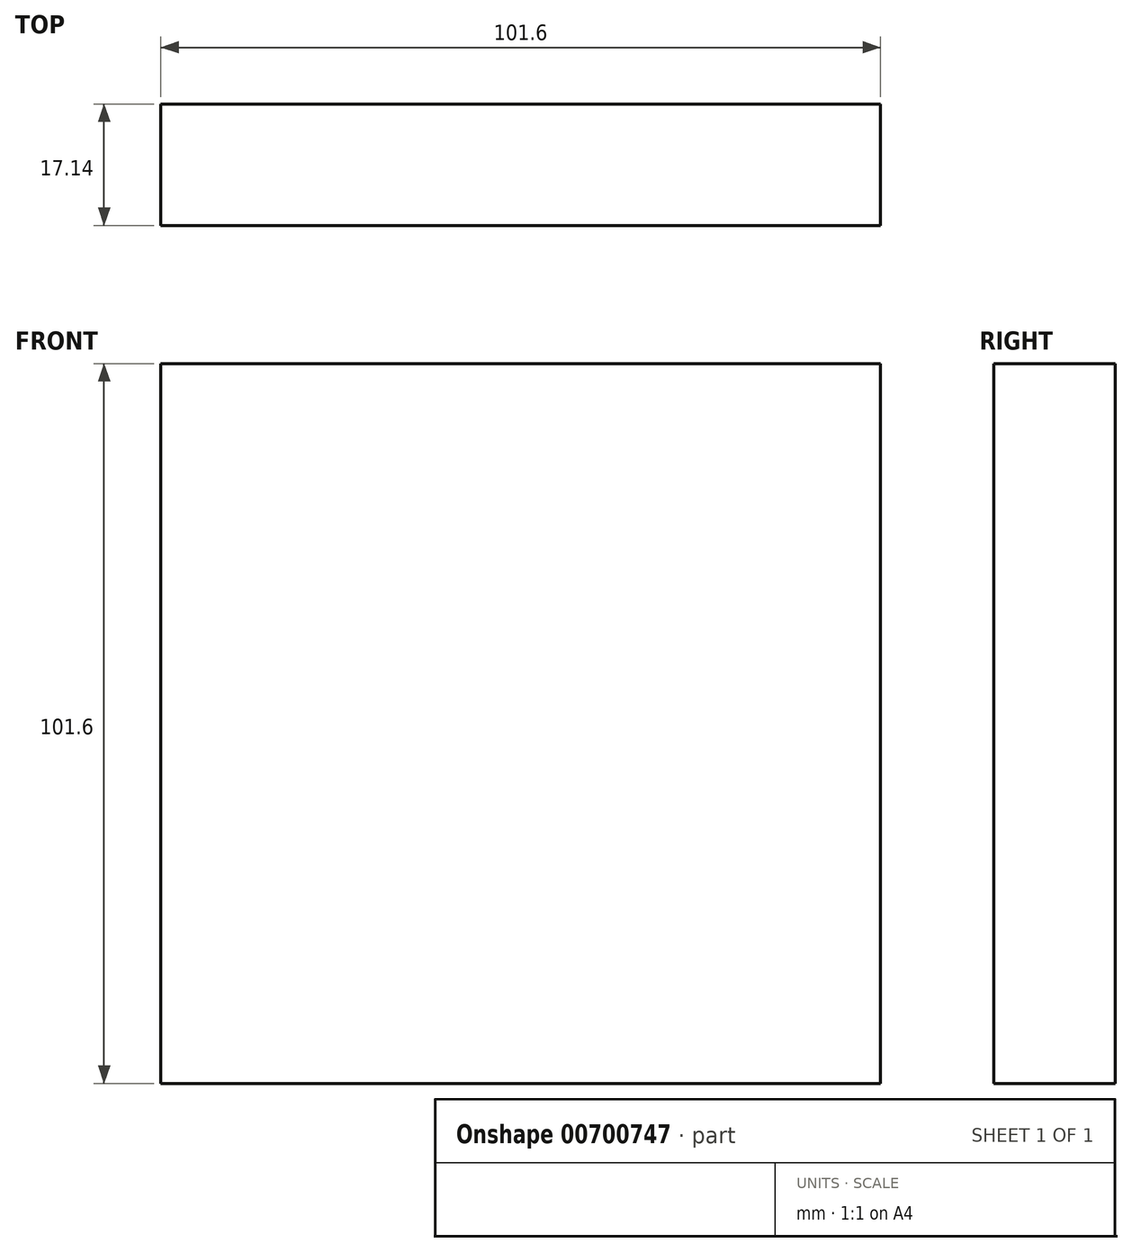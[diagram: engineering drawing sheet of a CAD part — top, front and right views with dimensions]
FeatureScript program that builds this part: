
annotation { "Feature Type Name" : "Feature", "Feature Type Description" : "" }
export const myFeature = defineFeature(function(context is Context, id is Id, definition is map)
    precondition{}
    {
        {
            var Q0;
            Q0=qCreatedBy(makeId("Front.planeOp"),FACE);
            var sketch = newSketch(context, id + "F0", { "sketchPlane" : qUnion([Q0])});
            skLineSegment(sketch, "E0.bottom", {"start": v(0, 0) * mm, "end": v(101.6, 0) * mm});
            skLineSegment(sketch, "E0.top", {"start": v(0, 101.6) * mm, "end": v(101.6, 101.6) * mm});
            skLineSegment(sketch, "E0.left", {"start": v(0, 0) * mm, "end": v(0, 101.6) * mm});
            skLineSegment(sketch, "E0.right", {"start": v(101.6, 0) * mm, "end": v(101.6, 101.6) * mm});
            skSolve(sketch);
        }
        {
            var Q0;
            Q0 = qSketchRegion(id + "F0", true);
            extrude(context, id + "F1", {"entities" : qUnion([Q0]), "depth" : 17.14 * mm, "offsetDistance" : 25.4 * mm});
        }
    });
